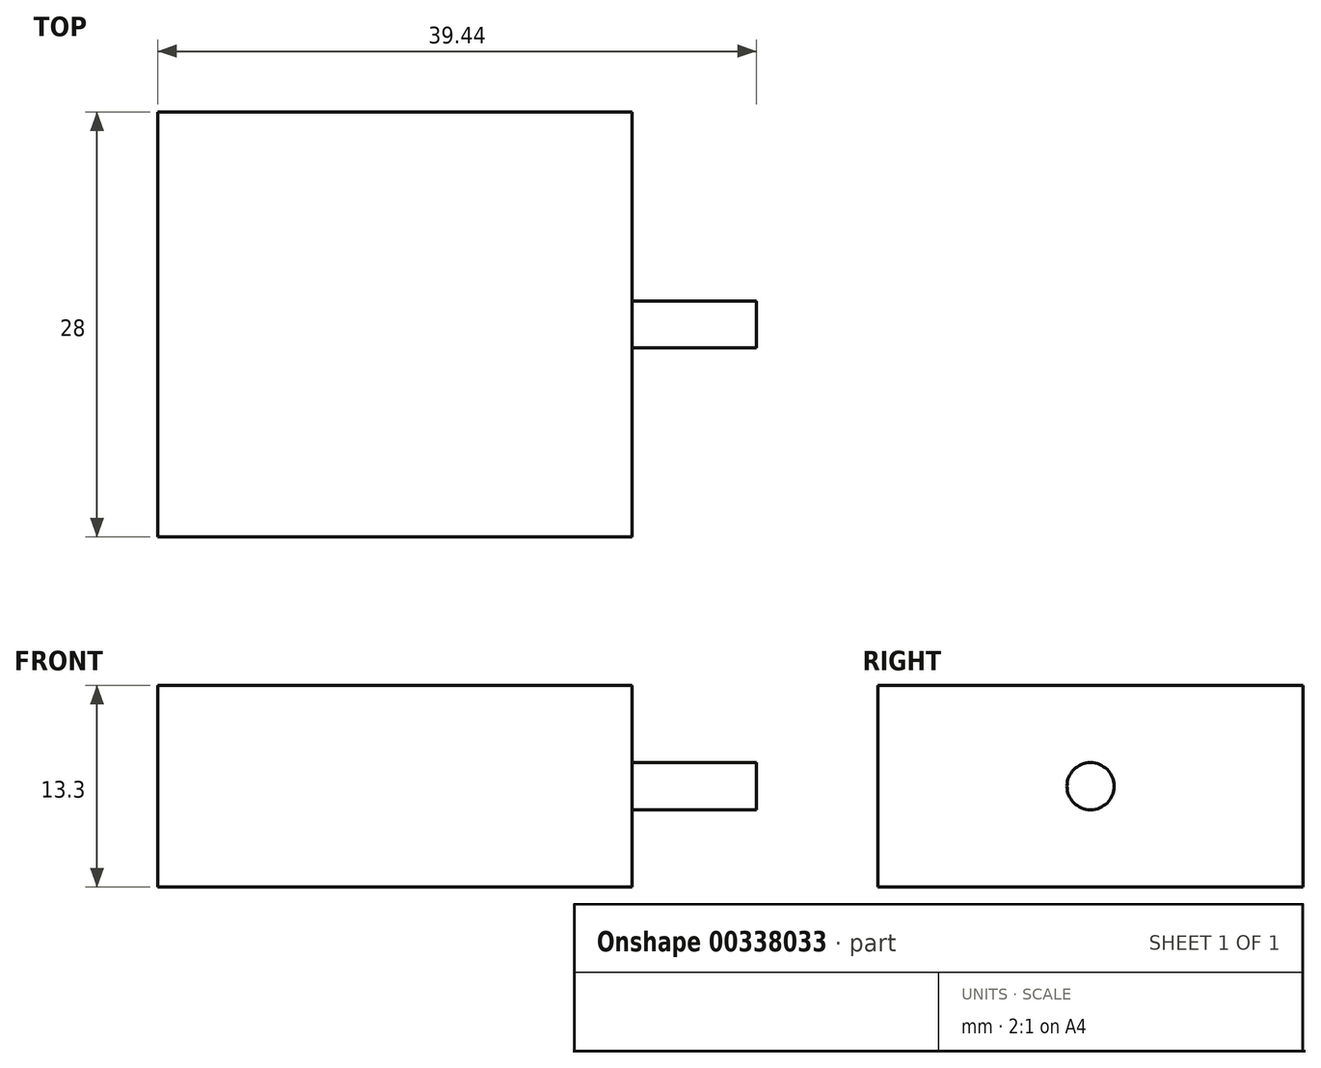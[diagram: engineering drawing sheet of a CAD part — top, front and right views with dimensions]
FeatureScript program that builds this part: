
annotation { "Feature Type Name" : "Feature", "Feature Type Description" : "" }
export const myFeature = defineFeature(function(context is Context, id is Id, definition is map)
    precondition{}
    {
        {
            var Q0;
            Q0=qCreatedBy(makeId("Top.planeOp"),FACE);
            var sketch = newSketch(context, id + "F0", { "sketchPlane" : qUnion([Q0])});
            skLineSegment(sketch, "E0.bottom", {"start": v(15.61, 14) * mm, "end": v(15.61, -14) * mm});
            skLineSegment(sketch, "E0.top", {"start": v(-15.61, 14) * mm, "end": v(-15.61, -14) * mm});
            skLineSegment(sketch, "E0.left", {"start": v(15.61, 14) * mm, "end": v(-15.61, 14) * mm});
            skLineSegment(sketch, "E0.right", {"start": v(15.61, -14) * mm, "end": v(-15.61, -14) * mm});
            skPoint(sketch, "E0.middle", {"position": v(0, 0) * mm});
            skSolve(sketch);
        }
        {
            var Q0;
            Q0=qSketchRegion(id+"F0",true);
            extrude(context, id + "F1", {"entities" : qUnion([Q0]), "depth" : 13.3 * mm});
        }
        {
            var Q0;
            Q0=makeQuery(id+"F1.opExtrude","SWEPT_FACE",FACE,{"disambiguationData":[OSD([sQuery(id+"F0.wireOp",EDGE,"E0.bottom")])]});
            var sketch = newSketch(context, id + "F2", { "sketchPlane" : qUnion([Q0])});
            skCircle(sketch, "E1", {"center": v(0, 6.65) * mm, "radius": 1.55 * mm});
            skSolve(sketch);
        }
        {
            var Q0;
            Q0=qSketchRegion(id+"F2",true);
            extrude(context, id + "F3", {"entities" : qUnion([Q0]), "operationType" : NewBodyOperationType.ADD, "depth" : 8.2 * mm});
        }
    });
